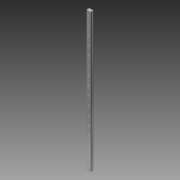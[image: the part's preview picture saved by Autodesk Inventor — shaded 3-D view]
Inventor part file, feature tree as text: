
AUTODESK INVENTOR PART (.ipt)
format: ipt  version: 2015 (Build 190159000, 159)  size: 136,192 bytes
history: native  units: mm
features: sketch x2, extrude x1, hole x1
ambient origin geometry x8: Origin, YZ Plane, XZ Plane, XY Plane, X Axis, Y Axis, Z Axis, Center Point
bodies: Solid1 (feature_tree)
feature tree (4):
  extrude  "Extrusion1"  Depth=7.5mm
  hole  "Hole1"  [1 undecoded]
  sketch  "Sketch1"  dims[d0=12.0mm d1=7.5mm]
  sketch  "Sketch2"  dims[d2=9.5mm d3=1.386995mm d4=4.0mm d5=400.0mm d6=0.0mm d7=12.0mm d8=160.0mm d10=25.0mm d11=10.0mm d13=10.0mm d15=4.0mm d16=6.0mm d17=6.0mm d18=4.5mm d19=90.0deg d20=8.0mm d21=20.594885mm]
note: 1 required parameter value undecoded (feature->parameter linkage not recoverable at this tier; creation-order binding heuristic only, values carry confidence <= 0.55)
